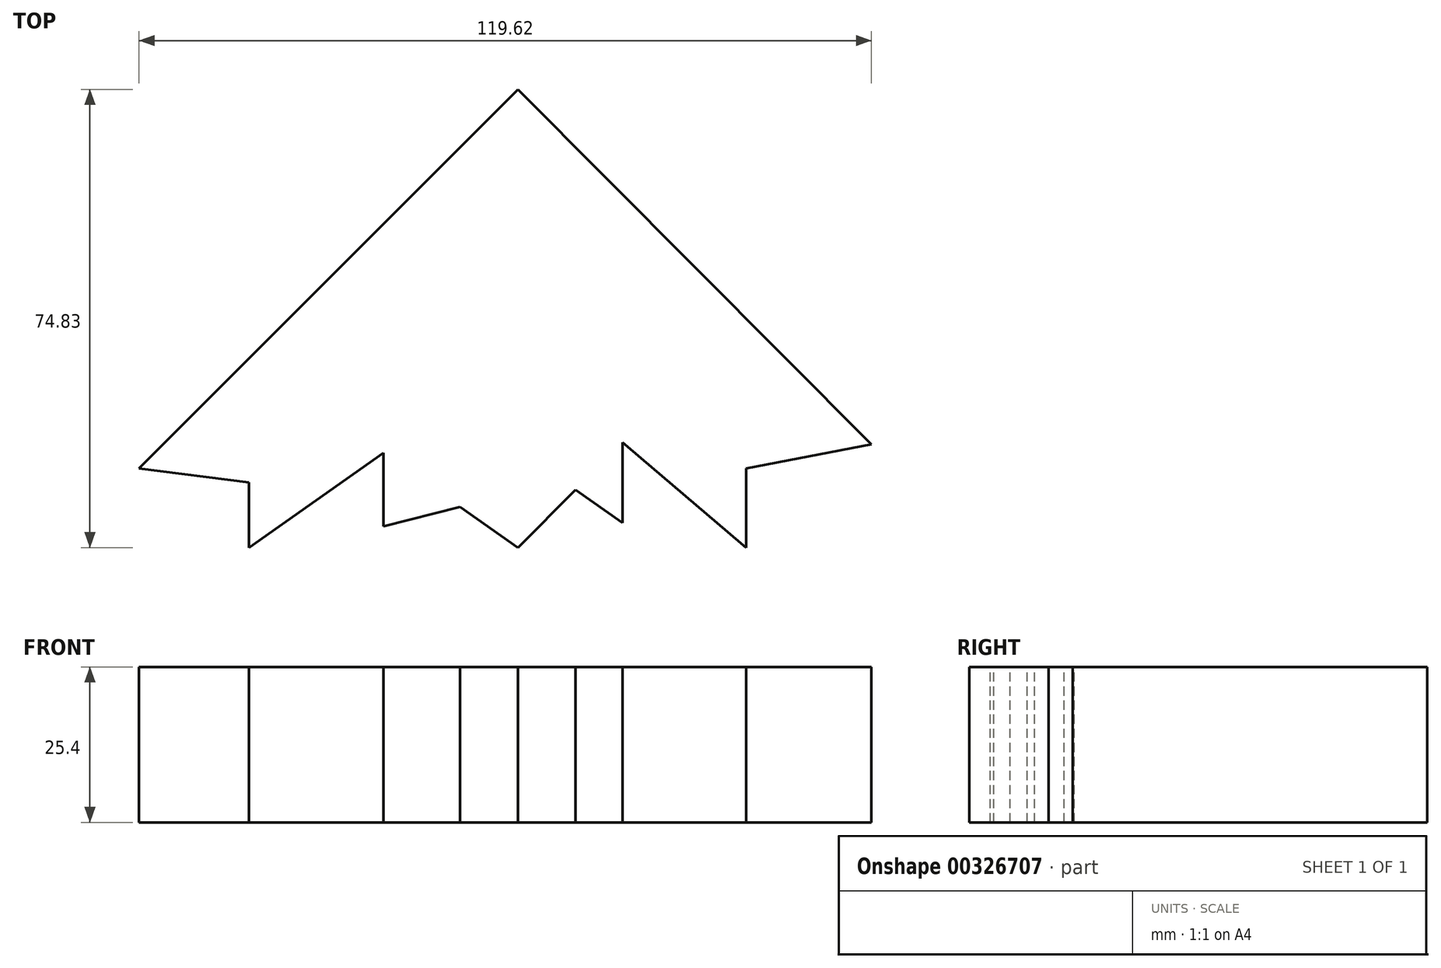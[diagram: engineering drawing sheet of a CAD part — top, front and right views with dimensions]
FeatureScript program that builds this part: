
annotation { "Feature Type Name" : "Feature", "Feature Type Description" : "" }
export const myFeature = defineFeature(function(context is Context, id is Id, definition is map)
    precondition{}
    {
        {
            var Q0;
            Q0=qCreatedBy(makeId("Top.planeOp"),FACE);
            var sketch = newSketch(context, id + "F0", { "sketchPlane" : qUnion([Q0])});
            skLineSegment(sketch, "E0", {"start": v(-74.83, 0) * mm, "end": v(0, 74.83) * mm});
            skLineSegment(sketch, "E1", {"start": v(74.54, 0) * mm, "end": v(0, 74.83) * mm});
            skLineSegment(sketch, "E2", {"start": v(0, 29.93) * mm, "end": v(-22.45, 52.38) * mm});
            skLineSegment(sketch, "E3", {"start": v(0, 29.93) * mm, "end": v(22.45, 52.3) * mm});
            skLineSegment(sketch, "E4", {"start": v(-43.9, 30.94) * mm, "end": v(0, 0) * mm});
            skLineSegment(sketch, "E5", {"start": v(37.27, 37.41) * mm, "end": v(0, 0) * mm});
            skLineSegment(sketch, "E6", {"start": v(0, -4.03) * mm, "end": v(0, 29.93) * mm});
            skLineSegment(sketch, "E7", {"start": v(-37.41, 37.41) * mm, "end": v(0, 12.95) * mm});
            skLineSegment(sketch, "E8", {"start": v(0, 12.95) * mm, "end": v(29.15, 45.56) * mm});
            skLineSegment(sketch, "E9", {"start": v(-43.9, 30.94) * mm, "end": v(-43.9, 0) * mm});
            skLineSegment(sketch, "E10", {"start": v(37.27, 37.41) * mm, "end": v(37.27, 0) * mm});
            skLineSegment(sketch, "E11", {"start": v(-21.95, 15.47) * mm, "end": v(-43.9, 0) * mm});
            skLineSegment(sketch, "E12", {"start": v(17.09, 17.16) * mm, "end": v(37.27, 0) * mm});
            skLineSegment(sketch, "E13", {"start": v(-43.9, 10.65) * mm, "end": v(-61.88, 12.95) * mm});
            skLineSegment(sketch, "E14", {"start": v(37.27, 12.95) * mm, "end": v(57.74, 16.87) * mm});
            skLineSegment(sketch, "E15", {"start": v(-21.95, 15.47) * mm, "end": v(-21.95, 0) * mm});
            skLineSegment(sketch, "E16", {"start": v(17.09, 17.16) * mm, "end": v(17.09, 0) * mm});
            skLineSegment(sketch, "E17", {"start": v(-21.95, 3.45) * mm, "end": v(-9.43, 6.65) * mm});
            skLineSegment(sketch, "E18", {"start": v(17.09, 4.03) * mm, "end": v(9.4, 9.44) * mm});
            skSolve(sketch);
        }
        {
            var Q0;
            {var subQ3=sQuery(id+"F0.wireOp",EDGE,"E2");Q0=makeQuery(id+"F0.imprint","IMPRINT",FACE,{"disambiguationData":[TD([[makeQuery(id+"F0.imprint","IMPRINT",EDGE,{"derivedFrom":subQ3}),-1.0]])]});}
            var Q1;
            {var subQ0=sQuery(id+"F0.wireOp",EDGE,"E2");Q1=makeQuery(id+"F0.imprint","IMPRINT",FACE,{"disambiguationData":[TD([[makeQuery(id+"F0.imprint","IMPRINT",EDGE,{"derivedFrom":subQ0}),1.0]])]});}
            var Q2;
            {var subQ0=sQuery(id+"F0.wireOp",EDGE,"E3");Q2=makeQuery(id+"F0.imprint","IMPRINT",FACE,{"disambiguationData":[TD([[makeQuery(id+"F0.imprint","IMPRINT",EDGE,{"derivedFrom":subQ0}),-1.0]])]});}
            var Q3;
            {var subQ7=sQuery(id+"F0.wireOp",EDGE,"E8");Q3=makeQuery(id+"F0.imprint","IMPRINT",FACE,{"disambiguationData":[TD([[makeQuery(id+"F0.imprint","IMPRINT",EDGE,{"derivedFrom":subQ7}),-1.0]])]});}
            var Q4;
            {var subQ6=sQuery(id+"F0.wireOp",EDGE,"E7");Q4=makeQuery(id+"F0.imprint","IMPRINT",FACE,{"disambiguationData":[TD([[makeQuery(id+"F0.imprint","IMPRINT",EDGE,{"derivedFrom":subQ6}),-1.0]])]});}
            var Q5;
            {var subQ3=sQuery(id+"F0.wireOp",EDGE,"E11");Q5=makeQuery(id+"F0.imprint","IMPRINT",FACE,{"disambiguationData":[TD([[makeQuery(id+"F0.imprint","IMPRINT",EDGE,{"derivedFrom":subQ3}),-1.0]])]});}
            var Q6;
            {var subQ3=sQuery(id+"F0.wireOp",EDGE,"E13");Q6=makeQuery(id+"F0.imprint","IMPRINT",FACE,{"disambiguationData":[TD([[makeQuery(id+"F0.imprint","IMPRINT",EDGE,{"derivedFrom":subQ3}),-1.0]])]});}
            var Q7;
            {var subQ3=sQuery(id+"F0.wireOp",EDGE,"E17");Q7=makeQuery(id+"F0.imprint","IMPRINT",FACE,{"disambiguationData":[TD([[makeQuery(id+"F0.imprint","IMPRINT",EDGE,{"derivedFrom":subQ3}),1.0]])]});}
            var Q8;
            {var subQ3=sQuery(id+"F0.wireOp",EDGE,"E18");Q8=makeQuery(id+"F0.imprint","IMPRINT",FACE,{"disambiguationData":[TD([[makeQuery(id+"F0.imprint","IMPRINT",EDGE,{"derivedFrom":subQ3}),-1.0]])]});}
            var Q9;
            {var subQ3=sQuery(id+"F0.wireOp",EDGE,"E12");Q9=makeQuery(id+"F0.imprint","IMPRINT",FACE,{"disambiguationData":[TD([[makeQuery(id+"F0.imprint","IMPRINT",EDGE,{"derivedFrom":subQ3}),1.0]])]});}
            var Q10;
            {var subQ3=sQuery(id+"F0.wireOp",EDGE,"E14");Q10=makeQuery(id+"F0.imprint","IMPRINT",FACE,{"disambiguationData":[TD([[makeQuery(id+"F0.imprint","IMPRINT",EDGE,{"derivedFrom":subQ3}),1.0]])]});}
            extrude(context, id + "F1", {"entities" : qUnion([Q0, Q1, Q2, Q3, Q4, Q5, Q6, Q7, Q8, Q9, Q10]), "oppositeDirection" : true, "depth" : 25.4 * mm});
        }
    });
